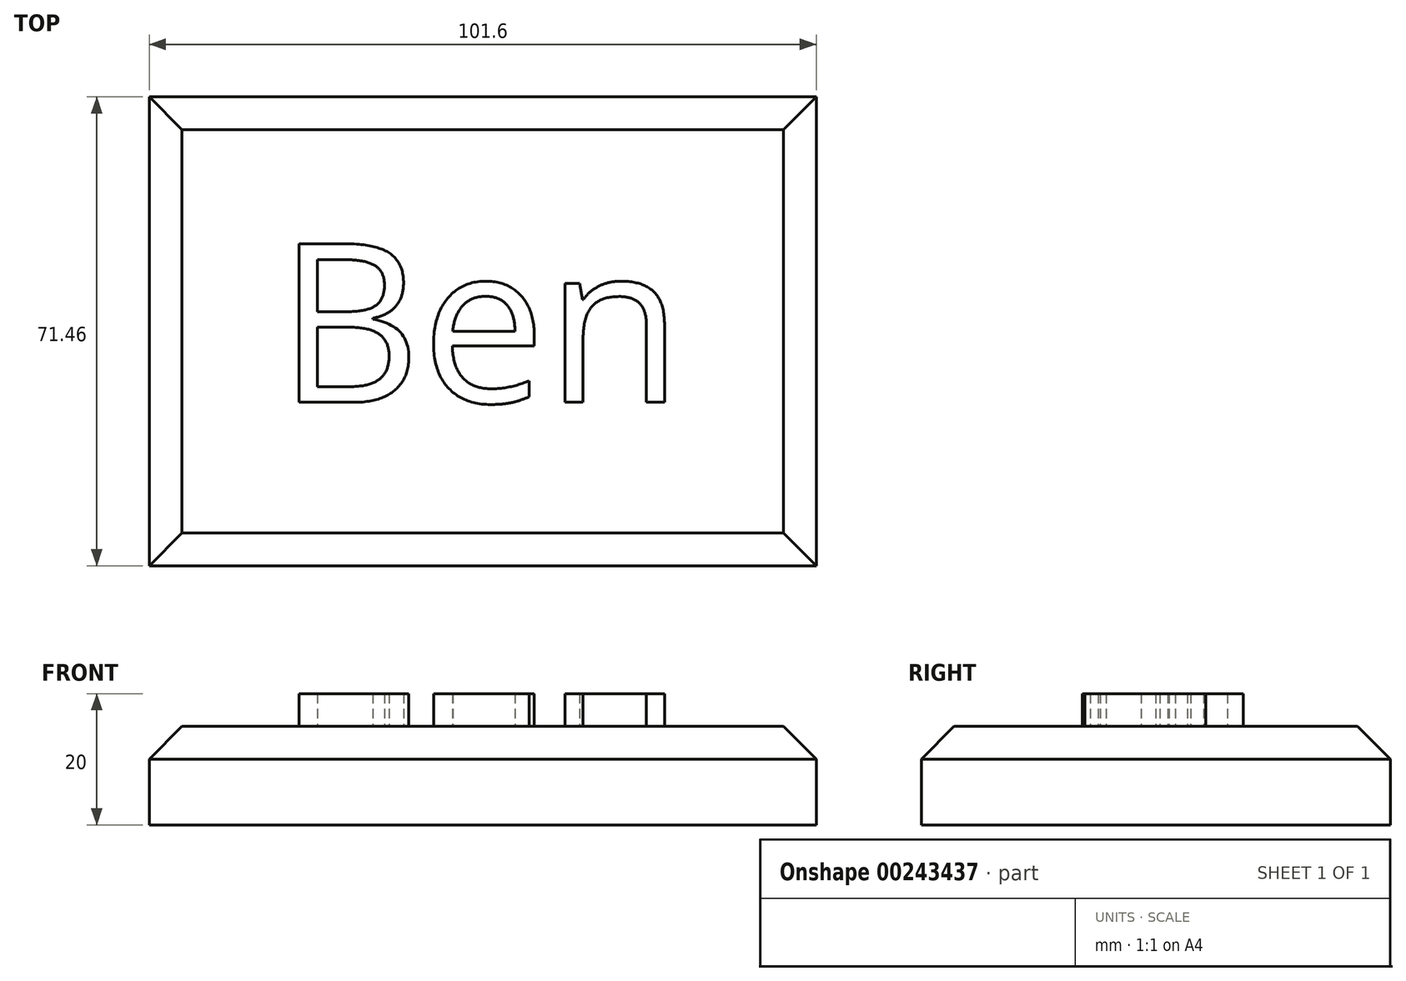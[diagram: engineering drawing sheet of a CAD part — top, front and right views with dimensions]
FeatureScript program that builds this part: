
annotation { "Feature Type Name" : "Feature", "Feature Type Description" : "" }
export const myFeature = defineFeature(function(context is Context, id is Id, definition is map)
    precondition{}
    {
        {
            var Q0;
            Q0=qCreatedBy(makeId("Top.planeOp"),FACE);
            var sketch = newSketch(context, id + "F0", { "sketchPlane" : qUnion([Q0])});
            skLineSegment(sketch, "E0.bottom", {"start": v(50.8, -35.73) * mm, "end": v(-50.8, -35.73) * mm});
            skLineSegment(sketch, "E0.top", {"start": v(50.8, 35.73) * mm, "end": v(-50.8, 35.73) * mm});
            skLineSegment(sketch, "E0.left", {"start": v(50.8, -35.73) * mm, "end": v(50.8, 35.73) * mm});
            skLineSegment(sketch, "E0.right", {"start": v(-50.8, -35.73) * mm, "end": v(-50.8, 35.73) * mm});
            skPoint(sketch, "E0.middle", {"position": v(0, 0) * mm});
            skSolve(sketch);
        }
        {
            var Q0;
            Q0 = qSketchRegion(id + "FTIoUKamMWdU0xV_1", true);
            var Q1;
            Q1=makeQuery(id+"F0.imprint","IMPRINT",FACE,{"disambiguationData":[TD([[makeQuery(id+"F0.imprint","IMPRINT",EDGE,{"derivedFrom":sQuery(id+"F0.wireOp",EDGE,"E0.bottom")}),-1.0]])]});
            extrude(context, id + "F1", {"entities" : qUnion([Q0, Q1]), "depth" : 15 * mm});
        }
        {
            var Q0;
            Q0=qCreatedBy(makeId("Top.planeOp"),FACE);
            var sketch = newSketch(context, id + "F2", { "sketchPlane" : qUnion([Q0])});
            skText(sketch, "E1", { "text": "Ben", "fontName": "OpenSans-Regular.ttf"});
            const initialGuessF2  = {"E1": [-0.03133, -0.01083, 1, 0, 0.02439]};
            skSetInitialGuess(sketch, initialGuessF2);
            skSolve(sketch);
        }
        {
            var Q0;
            Q0 = qSketchRegion(id + "F2", true);
            extrude(context, id + "F3", {"entities" : qUnion([Q0]), "operationType" : NewBodyOperationType.ADD, "depth" : 20 * mm});
        }
        {
            var Q0;
            Q0=makeQuery(id+"F1.opExtrude","CAP_EDGE",EDGE,{"disambiguationData":[OSD([sQuery(id+"F0.wireOp",EDGE,"E0.top")])],"isStart":false});
            var Q1;
            Q1=makeQuery(id+"F1.opExtrude","CAP_EDGE",EDGE,{"disambiguationData":[OSD([sQuery(id+"F0.wireOp",EDGE,"E0.left")])],"isStart":false});
            var Q2;
            Q2=makeQuery(id+"F1.opExtrude","CAP_EDGE",EDGE,{"disambiguationData":[OSD([sQuery(id+"F0.wireOp",EDGE,"E0.bottom")])],"isStart":false});
            var Q3;
            Q3=makeQuery(id+"F1.opExtrude","CAP_EDGE",EDGE,{"disambiguationData":[OSD([sQuery(id+"F0.wireOp",EDGE,"E0.right")])],"isStart":false});
            chamfer(context, id + "F4", {"entities" : qUnion([Q0, Q1, Q2, Q3]), "width" : 5 * mm, "tangentPropagation" : true});
        }
    });
